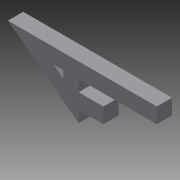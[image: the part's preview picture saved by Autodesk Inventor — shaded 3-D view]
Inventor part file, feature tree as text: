
AUTODESK INVENTOR PART (.ipt)
format: ipt  version: 2013 (Build 170138000, 138)  size: 91,136 bytes
history: native  units: in
note: dims shown in document units (in); Inventor stores cm internally (conversion verified against a paired STEP export)
features: extrude x1, sketch x1
ambient origin geometry x8: Origin, YZ Plane, XZ Plane, XY Plane, X Axis, Y Axis, Z Axis, Center Point
bodies: Solid1 (feature_tree)
feature tree (2):
  extrude  "Extrusion1"  Depth=3.5in
  sketch  "Sketch1"  dims[d0=6.25in d1=3.5in d2=1.625in d3=0.75in d4=1.0in d5=1.0in d6=1.0in d7=1.0in d8=1.0in d9=3.5in d10=1.0in d11=0.0in]
